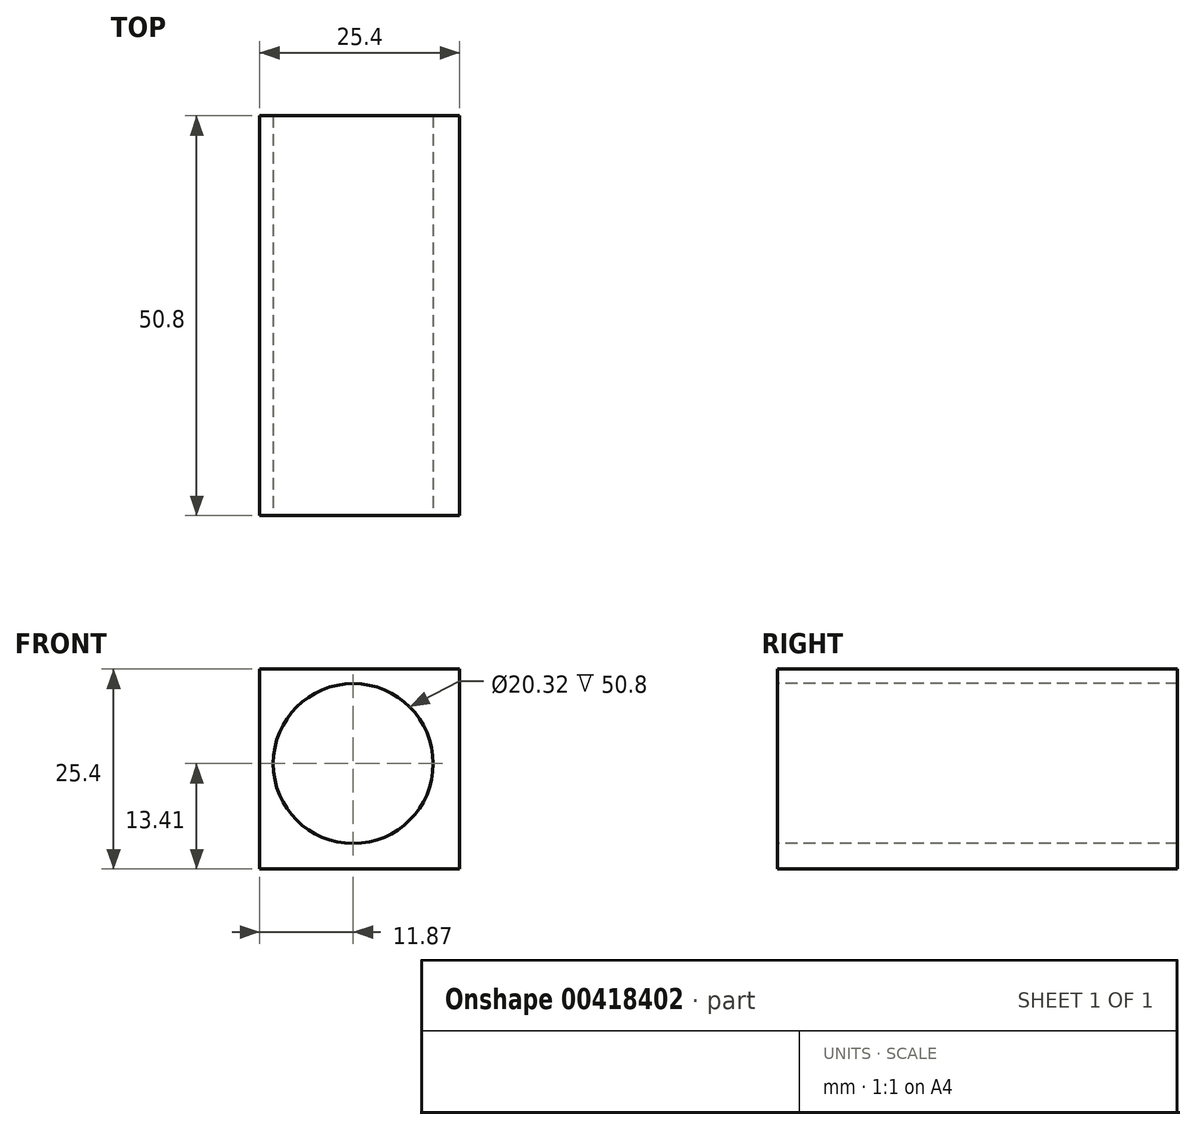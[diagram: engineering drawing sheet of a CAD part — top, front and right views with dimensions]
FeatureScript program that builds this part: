
annotation { "Feature Type Name" : "Feature", "Feature Type Description" : "" }
export const myFeature = defineFeature(function(context is Context, id is Id, definition is map)
    precondition{}
    {
        {
            var Q0;
            Q0=qCreatedBy(makeId("Front.planeOp"),FACE);
            var sketch = newSketch(context, id + "F0", { "sketchPlane" : qUnion([Q0])});
            skLineSegment(sketch, "E0.bottom", {"start": v(-11.87, 11.99) * mm, "end": v(13.53, 11.99) * mm});
            skLineSegment(sketch, "E0.top", {"start": v(-11.87, -13.41) * mm, "end": v(13.53, -13.41) * mm});
            skLineSegment(sketch, "E0.left", {"start": v(-11.87, 11.99) * mm, "end": v(-11.87, -13.41) * mm});
            skLineSegment(sketch, "E0.right", {"start": v(13.53, 11.99) * mm, "end": v(13.53, -13.41) * mm});
            skSolve(sketch);
        }
        {
            var Q0;
            Q0 = qSketchRegion(id + "F0", true);
            extrude(context, id + "F1", {"entities" : qUnion([Q0]), "depth" : 50.8 * mm});
        }
        {
            var Q0;
            Q0=makeQuery(id+"F1.opExtrude","CAP_FACE",FACE,{"disambiguationData":[OSD([sQuery(id+"F0.wireOp",EDGE,"E0.bottom"),sQuery(id+"F0.wireOp",EDGE,"E0.top"),sQuery(id+"F0.wireOp",EDGE,"E0.left"),sQuery(id+"F0.wireOp",EDGE,"E0.right")])],"isStart":false});
            var sketch = newSketch(context, id + "F2", { "sketchPlane" : qUnion([Q0])});
            skCircle(sketch, "E1", {"center": v(0, 0) * mm, "radius": 10.16 * mm});
            skSolve(sketch);
        }
        {
            var Q0;
            Q0=makeQuery(id+"F2.imprint","IMPRINT",FACE,{"disambiguationData":[TD([[makeQuery(id+"F2.imprint","IMPRINT",EDGE,{"derivedFrom":sQuery(id+"F2.wireOp",EDGE,"E1")}),1.0]])]});
            extrude(context, id + "F3", {"entities" : qUnion([Q0]), "operationType" : NewBodyOperationType.REMOVE, "endBound" : BoundingType.THROUGH_ALL, "oppositeDirection" : true, "depth" : 25.4 * mm});
        }
    });
